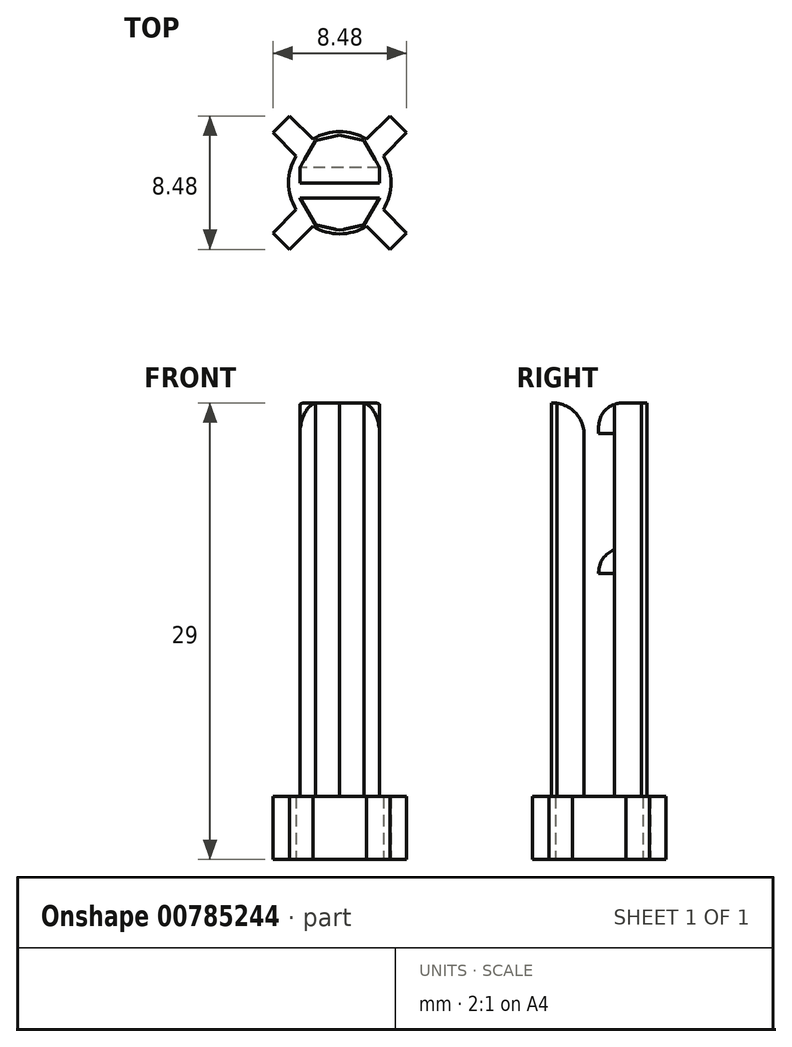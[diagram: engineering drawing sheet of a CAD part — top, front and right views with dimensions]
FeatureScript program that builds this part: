
annotation { "Feature Type Name" : "Feature", "Feature Type Description" : "" }
export const myFeature = defineFeature(function(context is Context, id is Id, definition is map)
    precondition{}
    {
        {
            var Q0;
            Q0=qCreatedBy(makeId("Top.planeOp"),FACE);
            var sketch = newSketch(context, id + "F0", { "sketchPlane" : qUnion([Q0])});
            skCircle(sketch, "E0", {"center": v(0, 0) * mm, "radius": 3.25 * mm});
            skLineSegment(sketch, "E1", {"start": v(-3.71, 3.71) * mm, "end": v(-4.24, 3.18) * mm});
            skLineSegment(sketch, "E2", {"start": v(-4.24, 3.18) * mm, "end": v(-2.77, 1.7) * mm});
            skLineSegment(sketch, "E3.MirrorCS", {"start": v(-3.71, 3.71) * mm, "end": v(-3.18, 4.24) * mm});
            skLineSegment(sketch, "E4.MirrorCS", {"start": v(-3.18, 4.24) * mm, "end": v(-1.7, 2.77) * mm});
            skLineSegment(sketch, "E5.MirrorCS", {"start": v(4.24, -3.18) * mm, "end": v(2.77, -1.7) * mm});
            skLineSegment(sketch, "E6.MirrorCS", {"start": v(3.71, -3.71) * mm, "end": v(3.18, -4.24) * mm});
            skLineSegment(sketch, "E7.MirrorCS", {"start": v(3.18, -4.24) * mm, "end": v(1.7, -2.77) * mm});
            skLineSegment(sketch, "E8.MirrorCS", {"start": v(3.71, -3.71) * mm, "end": v(4.24, -3.18) * mm});
            skLineSegment(sketch, "E9.MirrorCS", {"start": v(4.24, 3.18) * mm, "end": v(2.77, 1.7) * mm});
            skLineSegment(sketch, "E10.MirrorCS", {"start": v(3.71, 3.71) * mm, "end": v(4.24, 3.18) * mm});
            skLineSegment(sketch, "E11.MirrorCS", {"start": v(3.18, 4.24) * mm, "end": v(1.7, 2.77) * mm});
            skLineSegment(sketch, "E12.MirrorCS", {"start": v(3.71, 3.71) * mm, "end": v(3.18, 4.24) * mm});
            skLineSegment(sketch, "E13.MirrorCS", {"start": v(-4.24, -3.18) * mm, "end": v(-2.77, -1.7) * mm});
            skLineSegment(sketch, "E14.MirrorCS", {"start": v(-3.71, -3.71) * mm, "end": v(-4.24, -3.18) * mm});
            skLineSegment(sketch, "E15.MirrorCS", {"start": v(-3.18, -4.24) * mm, "end": v(-1.7, -2.77) * mm});
            skLineSegment(sketch, "E16.MirrorCS", {"start": v(-3.71, -3.71) * mm, "end": v(-3.18, -4.24) * mm});
            skSolve(sketch);
        }
        {
            var Q0;
            Q0 = qSketchRegion(id + "F0", true);
            extrude(context, id + "F1", {"entities" : qUnion([Q0]), "depth" : 4 * mm, "offsetDistance" : 25 * mm});
        }
        {
            var Q0;
            Q0=makeQuery(id+"F1.opExtrude","CAP_FACE",FACE,{"disambiguationData":[OSD([sQuery(id+"F0.wireOp",EDGE,"E0"),sQuery(id+"F0.wireOp",EDGE,"E1"),sQuery(id+"F0.wireOp",EDGE,"E2"),sQuery(id+"F0.wireOp",EDGE,"E3.MirrorCS"),sQuery(id+"F0.wireOp",EDGE,"E4.MirrorCS"),sQuery(id+"F0.wireOp",EDGE,"E5.MirrorCS"),sQuery(id+"F0.wireOp",EDGE,"E6.MirrorCS"),sQuery(id+"F0.wireOp",EDGE,"E7.MirrorCS"),sQuery(id+"F0.wireOp",EDGE,"E8.MirrorCS"),sQuery(id+"F0.wireOp",EDGE,"E9.MirrorCS"),sQuery(id+"F0.wireOp",EDGE,"E10.MirrorCS"),sQuery(id+"F0.wireOp",EDGE,"E11.MirrorCS"),sQuery(id+"F0.wireOp",EDGE,"E12.MirrorCS"),sQuery(id+"F0.wireOp",EDGE,"E13.MirrorCS"),sQuery(id+"F0.wireOp",EDGE,"E14.MirrorCS"),sQuery(id+"F0.wireOp",EDGE,"E15.MirrorCS"),sQuery(id+"F0.wireOp",EDGE,"E16.MirrorCS")])],"isStart":false});
            var sketch = newSketch(context, id + "F2", { "sketchPlane" : qUnion([Q0])});
            skLineSegment(sketch, "E17.bottom", {"start": v(-2.53, 0.96) * mm, "end": v(2.53, 0.96) * mm});
            skLineSegment(sketch, "E17.top", {"start": v(-2.53, -0.96) * mm, "end": v(2.53, -0.96) * mm});
            skPoint(sketch, "E17.middle", {"position": v(0, 0) * mm});
            skLineSegment(sketch, "E18", {"start": v(0, 3.02) * mm, "end": v(-1.55, 2.67) * mm});
            skLineSegment(sketch, "E19", {"start": v(-1.55, 2.67) * mm, "end": v(-2.53, 0.96) * mm});
            skLineSegment(sketch, "E20.MirrorCS", {"start": v(1.55, 2.67) * mm, "end": v(2.53, 0.96) * mm});
            skLineSegment(sketch, "E21.MirrorCS", {"start": v(0, 3.02) * mm, "end": v(1.55, 2.67) * mm});
            skLineSegment(sketch, "E22.MirrorCS", {"start": v(1.55, -2.67) * mm, "end": v(2.53, -0.96) * mm});
            skLineSegment(sketch, "E23.MirrorCS", {"start": v(0, -3.02) * mm, "end": v(1.55, -2.67) * mm});
            skLineSegment(sketch, "E24.MirrorCS", {"start": v(-1.55, -2.67) * mm, "end": v(-2.53, -0.96) * mm});
            skLineSegment(sketch, "E25.MirrorCS", {"start": v(0, -3.02) * mm, "end": v(-1.55, -2.67) * mm});
            skSolve(sketch);
        }
        {
            var Q0;
            Q0 = qSketchRegion(id + "F2", true);
            extrude(context, id + "F3", {"entities" : qUnion([Q0]), "operationType" : NewBodyOperationType.ADD, "depth" : 25 * mm, "offsetDistance" : 25 * mm});
        }
        {
            var Q0;
            Q0=makeQuery(id+"F3.opExtrude","CAP_EDGE",EDGE,{"disambiguationData":[OSD([sQuery(id+"F2.wireOp",EDGE,"E17.top")])],"isStart":false});
            fillet(context, id + "F4", {"entities" : qUnion([Q0]), "radius" : 2 * mm, "tangentPropagation" : true, "allowEdgeOverflow" : false});
        }
        {
            var Q0;
            Q0=makeQuery(id+"F3.opExtrude","SWEPT_FACE",FACE,{"disambiguationData":[OSD([sQuery(id+"F2.wireOp",EDGE,"E17.bottom")])]});
            var sketch = newSketch(context, id + "F5", { "sketchPlane" : qUnion([Q0])});
            skLineSegment(sketch, "E26.bottom", {"start": v(-2.53, 29) * mm, "end": v(2.53, 29) * mm});
            skLineSegment(sketch, "E26.top", {"start": v(-2.53, 27.07) * mm, "end": v(2.53, 27.07) * mm});
            skLineSegment(sketch, "E26.left", {"start": v(-2.53, 29) * mm, "end": v(-2.53, 27.07) * mm});
            skLineSegment(sketch, "E26.right", {"start": v(2.53, 29) * mm, "end": v(2.53, 27.07) * mm});
            skSolve(sketch);
        }
        {
            var Q0;
            Q0 = qSketchRegion(id + "F5", true);
            extrude(context, id + "F6", {"entities" : qUnion([Q0]), "operationType" : NewBodyOperationType.ADD, "depth" : 1 * mm, "offsetDistance" : 25 * mm});
        }
        {
            var Q0;
            Q0=makeQuery(id+"F6.opExtrude","CAP_EDGE",EDGE,{"disambiguationData":[OSD([sQuery(id+"F5.wireOp",EDGE,"E26.bottom")])],"isStart":false});
            fillet(context, id + "F7", {"entities" : qUnion([Q0]), "radius" : 1.5 * mm, "tangentPropagation" : true, "allowEdgeOverflow" : false});
        }
        {
            var Q0;
            Q0=makeQuery(id+"F3.opExtrude","SWEPT_FACE",FACE,{"disambiguationData":[OSD([sQuery(id+"F2.wireOp",EDGE,"E17.bottom")])]});
            var sketch = newSketch(context, id + "F8", { "sketchPlane" : qUnion([Q0])});
            skLineSegment(sketch, "E27.bottom", {"start": v(2.53, 19.66) * mm, "end": v(-2.53, 19.66) * mm});
            skLineSegment(sketch, "E27.top", {"start": v(2.53, 18.17) * mm, "end": v(-2.53, 18.17) * mm});
            skLineSegment(sketch, "E27.left", {"start": v(2.53, 19.66) * mm, "end": v(2.53, 18.17) * mm});
            skLineSegment(sketch, "E27.right", {"start": v(-2.53, 19.66) * mm, "end": v(-2.53, 18.17) * mm});
            skSolve(sketch);
        }
        {
            var Q0;
            Q0 = qSketchRegion(id + "F8", true);
            extrude(context, id + "F9", {"entities" : qUnion([Q0]), "operationType" : NewBodyOperationType.ADD, "depth" : 1 * mm, "offsetDistance" : 25 * mm});
        }
        {
            var Q0;
            Q0=makeQuery(id+"F9.opExtrude","CAP_EDGE",EDGE,{"disambiguationData":[OSD([sQuery(id+"F8.wireOp",EDGE,"E27.bottom")])],"isStart":false});
            fillet(context, id + "F10", {"entities" : qUnion([Q0]), "radius" : 1.5 * mm, "tangentPropagation" : true, "allowEdgeOverflow" : false});
        }
    });
